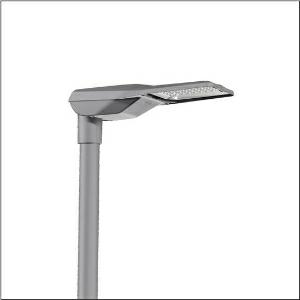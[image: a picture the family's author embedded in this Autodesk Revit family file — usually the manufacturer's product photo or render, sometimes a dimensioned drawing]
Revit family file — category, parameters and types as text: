
# Revit family: streetlight_sl_21_iq_mini___p0_8ab_5xe2r31d08jb_fb45
name_source: partatom
category: Lighting Fixtures
units: mm (PartAtom-declared; Revit-internal decimal feet)

## family parameters
Cut with Voids When Loaded = No
Host = Face
Light Source = No
Part Type = Normal
Room Calculation Point = No
Round Connector Dimension = Use Diameter
Shared = No

## types (1)
- --- (1 x LED, 9400 lm, 71.6 W, 3000K)
    Apparent Load = 72 VA
    CIE Flux Codes = 39 72 97 100 100
    Color Rendering = 70
    Color Temperature = 3000K
    Default Elevation = 1800 mm
    Description = Streetlight SL 21 iQ mini, mast luminaire, primary light control with lens, of PMMA, primary optical cover: cover, of toughened safety glass, transparent, light distribution: P0.8aB, light emission: direct distribution, primary light characteristic: asymmetric, installation type: post-top, side-entry, LED, High Power LED, rated luminous flux: 9.400lm, luminous efficacy: 131lm/W, light colour: 730, colour temperature: 3000K, control gear: iQ-Comfort, control: pre-setting: linear dimming characteristic, Auto-Match, Temp-Guard, Lumen-Switch, Night-Set, Smart-Wire, Light-Fading, Desk-Remote (wireless, voltage-free reading and setting of iQ features in the workshop via application-optimized NFC function/RFID function), optimised constant luminous flux control (CLO 2.0), mains connection: 220..240V, AC, 50/60Hz, start of lifetime: 72W, end of service life: 75W, reduction: 33W, luminaire housing, of diecast aluminium, powder-coated, Siteco® metallic grey (DB 702S), corrosivity category C5 mid according to DIN EN ISO 12944, please order mast flange separately, inclination adjustable: 0°, 5°, 10°, 15°, sealing non-destructively replaceable, multi-level sealing system, length: 628mm, width: 235mm, height: 110mm, mast flange for spigot size: 42mm (side-entry): 5XC10008XM4, 60/48mm (side-entry/post-top): 5XC10108XM2, 76/60mm (side-entry/post-top): 5XC10108XM1, mounting height: 4..8m, protection rating (complete): IP66, insulation class (complete): insulation class II (safety insulation), certification: CE, ENEC, ENEC+, VDE, impact resistance: IK10, permissible operating ambient temperature for outdoor applications: -40..+50°C, standard-compliant lighting for roads and squares, packaging unit: 1 piece

Light Distribution: P0.8aB
    Height = 110 mm
    Lamp = 1 x LED
    Lamp Light Flux = 9400 lm
    Lamp Power = 71.6 W
    Lamp count = 1
    Length = 625 mm
    Luminous efficacy = 131 lm/W
    Manufacturer = Siteco
    ModVariant = No
    Model = 5XE2R31D08JB
    Number of Poles = 1
    OnlyDefault = Yes
    Power Factor = 1
    Product Name = Streetlight SL 21 iQ mini | P0.8aB
    Product group = mast luminaire | pylon top
    ProductGroupID = 6100
    Protection Class = Protection class II
    Protection Degree = IP 66
    RLX_Detail_Level = 1
    RLX_Emergency_Light_Flux = 0 lm
    RLX_Emergency_Type = 0
    RLX_Emergency_Type_DB = No
    RlxData = <blob elided: 92029 chars, md5=d69e3d3c>
    Socket = socket
    Standby Power = 0 W
    System Light Flux = 9400 lm
    System Power = 72 W
    Type Comments = factory setting: luminous flux: 100 % | dim-lin: 254 | 746 mA
    Type Image = l_1003519.jpg
    URL = http://relux.com
    VarID = @adj_092659
    Voltage = 0 V
    Weight = 0.00 kg
    Width = 234 mm

## geometry (parser evidence)
native form markers: Blend x4, Sweep x12
no freeform markers — native parametric forms only
